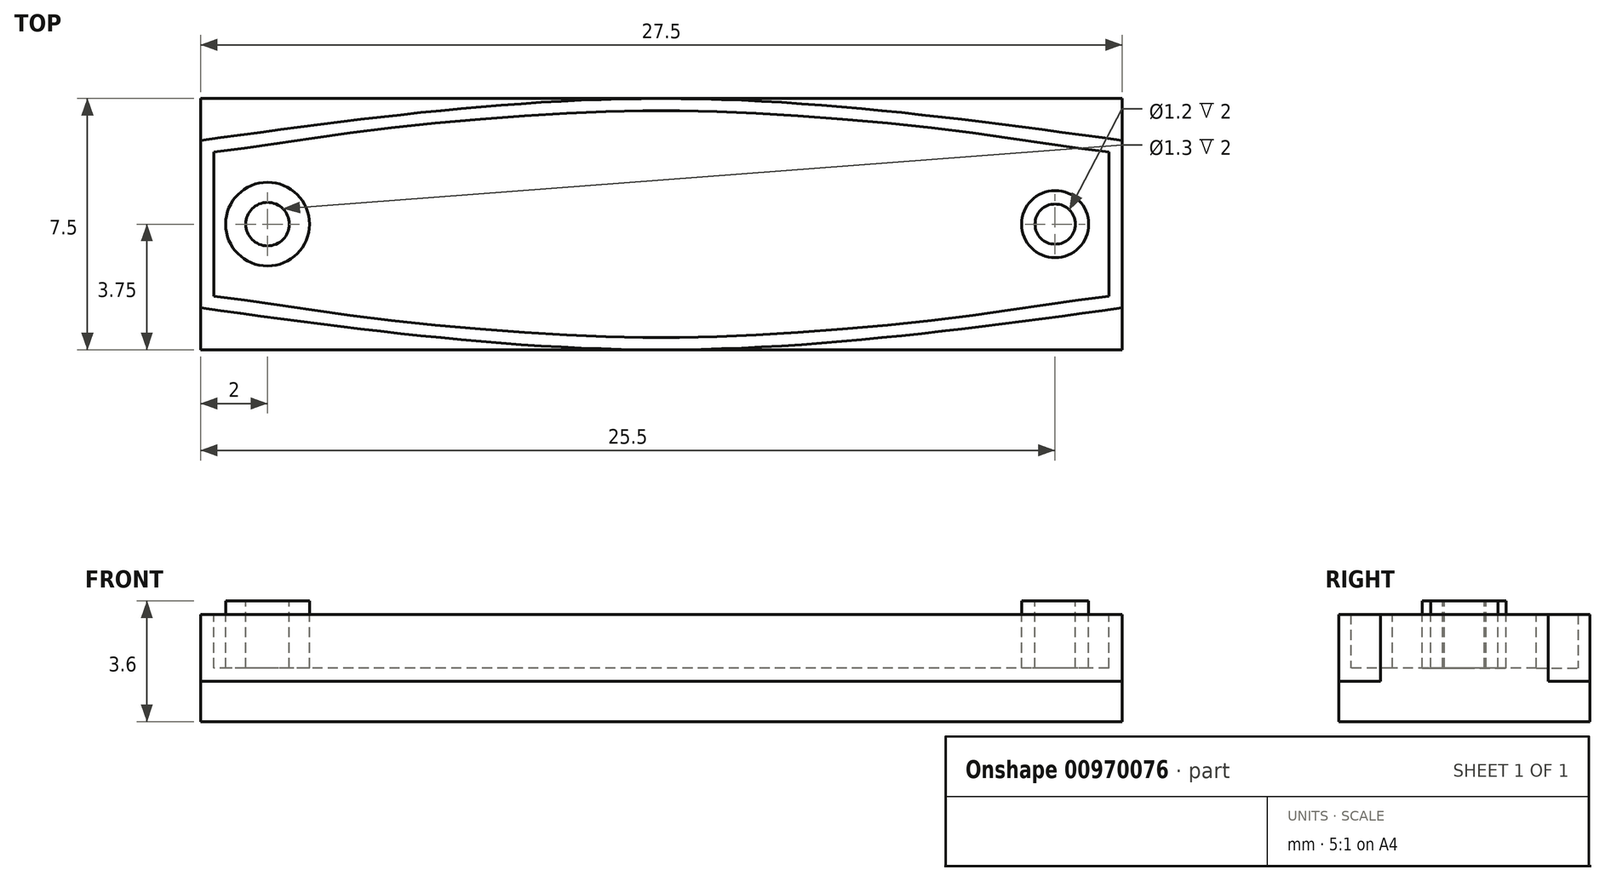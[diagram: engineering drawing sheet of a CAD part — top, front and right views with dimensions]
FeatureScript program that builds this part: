
annotation { "Feature Type Name" : "Feature", "Feature Type Description" : "" }
export const myFeature = defineFeature(function(context is Context, id is Id, definition is map)
    precondition{}
    {
        {
            var Q0;
            Q0=qCreatedBy(makeId("Top.planeOp"),FACE);
            var sketch = newSketch(context, id + "F0", { "sketchPlane" : qUnion([Q0])});
            skLineSegment(sketch, "E0.bottom", {"start": v(13.75, 3.75) * mm, "end": v(-13.75, 3.75) * mm});
            skLineSegment(sketch, "E0.top", {"start": v(13.75, -3.75) * mm, "end": v(-13.75, -3.75) * mm});
            skLineSegment(sketch, "E0.left", {"start": v(13.75, 3.75) * mm, "end": v(13.75, -3.75) * mm});
            skLineSegment(sketch, "E0.right", {"start": v(-13.75, 3.75) * mm, "end": v(-13.75, -3.75) * mm});
            skPoint(sketch, "E0.middle", {"position": v(0, 0) * mm});
            skSolve(sketch);
        }
        {
            var Q0;
            Q0=makeQuery(id+"F0.imprint","IMPRINT",FACE,{"disambiguationData":[TD([[makeQuery(id+"F0.imprint","IMPRINT",EDGE,{"derivedFrom":sQuery(id+"F0.wireOp",EDGE,"E0.bottom")}),1.0]])]});
            extrude(context, id + "F1", {"entities" : qUnion([Q0]), "depth" : 1.2 * mm, "offsetDistance" : 25.4 * mm});
        }
        {
            var Q0;
            Q0=makeQuery(id+"F1.opExtrude","CAP_FACE",FACE,{"disambiguationData":[OSD([sQuery(id+"F0.wireOp",EDGE,"E0.bottom"),sQuery(id+"F0.wireOp",EDGE,"E0.top"),sQuery(id+"F0.wireOp",EDGE,"E0.left"),sQuery(id+"F0.wireOp",EDGE,"E0.right")])],"isStart":false});
            var sketch = newSketch(context, id + "F2", { "sketchPlane" : qUnion([Q0])});
            skLineSegment(sketch, "E1.bottom", {"start": v(13.75, 3.75) * mm, "end": v(-13.75, 3.75) * mm});
            skLineSegment(sketch, "E1.top", {"start": v(13.75, -3.75) * mm, "end": v(-13.75, -3.75) * mm});
            skLineSegment(sketch, "E1.left", {"start": v(13.75, 3.75) * mm, "end": v(13.75, -3.75) * mm});
            skLineSegment(sketch, "E1.right", {"start": v(-13.75, 3.75) * mm, "end": v(-13.75, -3.75) * mm});
            skPoint(sketch, "E1.middle", {"position": v(0, 0) * mm});
            skLineSegment(sketch, "E2.bottom", {"start": v(13.75, 2.5) * mm, "end": v(-13.75, 2.5) * mm});
            skLineSegment(sketch, "E2.top", {"start": v(13.75, -2.5) * mm, "end": v(-13.75, -2.5) * mm});
            skLineSegment(sketch, "E2.left", {"start": v(13.75, 2.5) * mm, "end": v(13.75, -2.5) * mm});
            skLineSegment(sketch, "E2.right", {"start": v(-13.75, 2.5) * mm, "end": v(-13.75, -2.5) * mm});
            skFitSpline(sketch, "E3", {"points": [v(-13.75, 2.5) * mm, v(0, 3.75) * mm, v(13.75, 2.5) * mm], "startDerivative": vector(27.5, 3.75) * mm, "endDerivative": vector(27.5, -3.75) * mm});
            skFitSpline(sketch, "E4", {"points": [v(13.75, -2.5) * mm, v(0, -3.75) * mm, v(-13.75, -2.5) * mm], "startDerivative": vector(-27.5, -3.75) * mm, "endDerivative": vector(-27.5, 3.75) * mm});
            skSolve(sketch);
        }
        {
            var Q0;
            Q0=makeQuery(id+"F2.imprint","IMPRINT",FACE,{"disambiguationData":[TD([[makeQuery(id+"F2.imprint","IMPRINT",EDGE,{"derivedFrom":sQuery(id+"F2.wireOp",EDGE,"E2.bottom")}),1.0]])]});
            var Q1;
            {var subQ0=sQuery(id+"F2.wireOp",EDGE,"E2.bottom");Q1=makeQuery(id+"F2.imprint","IMPRINT",FACE,{"disambiguationData":[TD([[makeQuery(id+"F2.imprint","IMPRINT",EDGE,{"derivedFrom":subQ0}),-1.0]])]});}
            var Q2;
            {var subQ0=sQuery(id+"F2.wireOp",EDGE,"E2.top");Q2=makeQuery(id+"F2.imprint","IMPRINT",FACE,{"disambiguationData":[TD([[makeQuery(id+"F2.imprint","IMPRINT",EDGE,{"derivedFrom":subQ0}),1.0]])]});}
            extrude(context, id + "F3", {"entities" : qUnion([Q0, Q1, Q2]), "operationType" : NewBodyOperationType.ADD, "depth" : 2.4 * mm, "offsetDistance" : 25.4 * mm});
        }
        {
            var Q0;
            Q0=makeQuery(id+"F3.opExtrude","CAP_FACE",FACE,{"disambiguationData":[OSD([sQuery(id+"F2.wireOp",EDGE,"E2.left"),sQuery(id+"F2.wireOp",EDGE,"E2.right"),sQuery(id+"F2.wireOp",EDGE,"E3"),sQuery(id+"F2.wireOp",EDGE,"E4")])],"isStart":false});
            var sketch = newSketch(context, id + "F4", { "sketchPlane" : qUnion([Q0])});
            skCircle(sketch, "E5", {"center": v(11.75, 0) * mm, "radius": 1 * mm});
            skCircle(sketch, "E6", {"center": v(11.75, 0) * mm, "radius": 0.6 * mm});
            skCircle(sketch, "E7", {"center": v(-11.75, 0) * mm, "radius": 1.25 * mm});
            skCircle(sketch, "E8", {"center": v(-11.75, 0) * mm, "radius": 0.65 * mm});
            skFitSpline(sketch, "E9.0", {"points": [v(13.7, -2.1) * mm, v(11.4, -2.42) * mm, v(7.97, -2.88) * mm, v(3.41, -3.27) * mm, v(0, -3.39) * mm, v(-3.41, -3.27) * mm, v(-7.97, -2.88) * mm, v(-11.4, -2.42) * mm, v(-13.7, -2.1) * mm]});
            skFitSpline(sketch, "E10.0", {"points": [v(-13.7, 2.1) * mm, v(-11.4, 2.42) * mm, v(-7.97, 2.88) * mm, v(-3.41, 3.27) * mm, v(0, 3.39) * mm, v(3.41, 3.27) * mm, v(7.97, 2.88) * mm, v(11.4, 2.42) * mm, v(13.7, 2.1) * mm]});
            skLineSegment(sketch, "E11.0", {"start": v(13.35, 2.5) * mm, "end": v(13.35, -2.5) * mm});
            skLineSegment(sketch, "E12.0", {"start": v(-13.35, 2.5) * mm, "end": v(-13.35, -2.5) * mm});
            skSolve(sketch);
        }
        {
            var Q0;
            Q0=makeQuery(id+"F4.imprint","IMPRINT",FACE,{"disambiguationData":[TD([[makeQuery(id+"F4.imprint","IMPRINT",EDGE,{"derivedFrom":sQuery(id+"F4.wireOp",EDGE,"E5")}),-1.0]])]});
            var Q1;
            Q1=makeQuery(id+"F4.imprint","IMPRINT",FACE,{"disambiguationData":[TD([[makeQuery(id+"F4.imprint","IMPRINT",EDGE,{"derivedFrom":sQuery(id+"F4.wireOp",EDGE,"E8")}),1.0]])]});
            var Q2;
            Q2=makeQuery(id+"F4.imprint","IMPRINT",FACE,{"disambiguationData":[TD([[makeQuery(id+"F4.imprint","IMPRINT",EDGE,{"derivedFrom":sQuery(id+"F4.wireOp",EDGE,"E6")}),1.0]])]});
            extrude(context, id + "F5", {"entities" : qUnion([Q0, Q1, Q2]), "operationType" : NewBodyOperationType.REMOVE, "oppositeDirection" : true, "depth" : 2 * mm, "offsetDistance" : 25.4 * mm});
        }
        {
            var Q0;
            {var subQ0=sQuery(id+"F2.wireOp",EDGE,"E2.right");var subQ1=sQuery(id+"F2.wireOp",EDGE,"E2.left");var subQ2=sQuery(id+"F2.wireOp",EDGE,"E3");var subQ3=sQuery(id+"F2.wireOp",EDGE,"E4");Q0=makeQuery(id+"F5.boolean.opBoolean","SPLIT",FACE,{"disambiguationData":[TD([makeQuery(id+"F1.opExtrude","SWEPT_FACE",FACE,{"disambiguationData":[OSD([sQuery(id+"F0.wireOp",EDGE,"E0.left")])]})])],"derivedFrom":makeQuery(id+"F3.opExtrude","CAP_FACE",FACE,{"disambiguationData":[OSD([subQ1,subQ0,subQ2,subQ3])],"isStart":false})});}
            extrude(context, id + "F6", {"entities" : qUnion([Q0]), "operationType" : NewBodyOperationType.REMOVE, "oppositeDirection" : true, "depth" : .4 * mm, "offsetDistance" : 25.4 * mm});
        }
    });
